# Revit family: BuroSeating_Konfurb Neo 4 Leg Wood Base
name_source: partatom
category: Furniture
units: mm (PartAtom-declared; Revit-internal decimal feet)

## family parameters
Always vertical = Yes
Cut with Voids When Loaded = No
OmniClass Number = 23.40.70.14.64.11
OmniClass Title = Office Furniture
Room Calculation Point = No
Shared = No
Work Plane-Based = No

## types (2) — shared parameters
Assembly Code = E2020
BaseOffset = 18 mm  [stored 0.0590551 ft]
FeetMaterial = BuroSeating_Wood_Yellow Pine
Manufacturer = Buro Seating
NominalDepth = 630 mm  [stored 2.06693 ft]
NominalHeight = 855 mm  [stored 2.80512 ft]
NominalWidth = 680 mm  [stored 2.23097 ft]
ProductGroup = Konfurb Halo
ProductPageURL AU = https://buroseating.com
ProductPageURL NZ = https://buroseating.co.nz
ProductRange = Konfurb
SeatHeight = 410 mm  [stored 1.34514 ft]
URL = https://buroseating.co.nz
URL AU = https://buroseating.com
WarrantyDescription = Full 5 year guarantee (excluding upholstery)
zero-valued in all types: Default Elevation

## per-type parameters (varying)
| type | Description |
| KON702-B24-122 | Konfurb Neo 4 Leg Wood Base (Keylargo, Ash) |
| KON702-B24 | Konfurb Neo 4 Leg Wood Base (Custom) |

note: column(s) folded — value = type name in every type: Model

note: [stored X ft] marks values corroborated as IEEE doubles in the binary element streams (Revit-internal decimal feet)

## geometry (parser evidence)
native form markers: Sweep x5
no freeform markers — native parametric forms only
